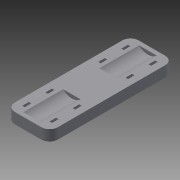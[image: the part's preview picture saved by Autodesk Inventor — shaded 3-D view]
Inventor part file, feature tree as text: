
AUTODESK INVENTOR PART (.ipt)
format: ipt  version: 2013 (Build 170138000, 138)  size: 153,088 bytes
history: native  units: mm
features: extrude x4, sketch x4, mirror x1, fillet x1
ambient origin geometry x8: Origin, YZ Plane, XZ Plane, XY Plane, X Axis, Y Axis, Z Axis, Center Point
bodies: Solid1 (feature_tree)
feature tree (10):
  extrude  "Extrusion1"  Depth=75.0mm
  extrude  "Extrusion2"  Depth=35.0mm
  extrude  "Extrusion3"  Depth=15.0mm
  mirror  "Mirror1"
  extrude  "Extrusion4"  Depth=6.477mm TaperAngle=0.0deg
  fillet  "Fillet1"  Radius=4.0mm
  sketch  "Sketch1"  dims[d0=26.0mm d2=75.0mm]
  sketch  "Sketch2"  dims[d3=6.477mm d4=0.0mm d5=35.0mm]
  sketch  "Sketch3"  dims[d6=45.0deg d7=15.0mm]
  sketch  "Sketch4"  dims[d8=24.0mm d9=6.477mm d10=0.0mm d11=4.0mm d13=1.5mm d14=15.0mm d15=5.0mm d16=6.477mm d17=0.0mm d18=15.0mm d20=6.477mm d21=0.0mm d22=5.0mm]
